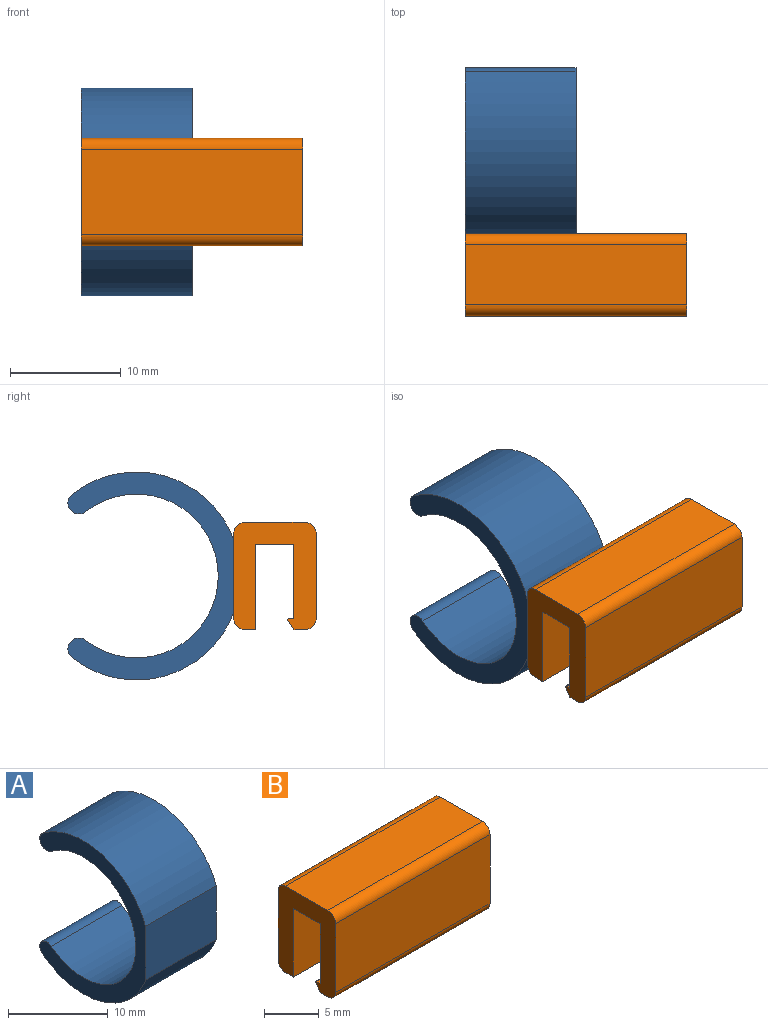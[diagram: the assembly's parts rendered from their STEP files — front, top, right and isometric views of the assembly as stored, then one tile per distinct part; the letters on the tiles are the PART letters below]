
ASSEMBLY  parts=2 mates=1
PART A: 8 faces, bbox 10x15x18.8 mm
  f0: cylinder r=9.4mm len=14.61mm, axis (-1,0,0), area 176.5mm2, adj f3,f4,f5,f7
  f1: cylinder r=9.4mm len=14.61mm, axis (-1,0,0), area 176.5mm2, adj f3,f4,f6,f7
  f2: cylinder r=7.4mm len=14.8mm, axis (-1,0,0), area 331.1mm2, adj f3,f4,f5,f6
  f3: plane 18.8x14.99mm, normal (1,0,0), area 75.6mm2, adj f0,f1,f2,f5,f6,f7
  f4: plane 18.8x14.99mm, normal (-1,0,0), area 75.6mm2, adj f0,f1,f2,f5,f6,f7
  f5: cylinder r=1mm len=10mm, axis (-1,0,0), area 31.4mm2, adj f0,f2,f3,f4
  f6: cylinder r=1mm len=10mm, axis (-1,0,0), area 31.4mm2, adj f1,f2,f3,f4
  f7: plane 10x6.61mm, normal (0,-1,0), area 66.1mm2, adj f0,f1,f3,f4
PART B: 17 faces, bbox 20x7.5x9.7 mm
  f0: plane 20x1mm, normal (0,0,-1), area 20mm2, adj f1,f10,f11,f16
  f1: plane 20x0.85mm, normal (0,0.84,-0.54), area 20.2mm2, adj f0,f10,f11,f12
  f2: plane 20x0.47mm, normal (0,0,1), area 9.3mm2, adj f3,f10,f11,f12
  f3: plane 20x6.7mm, normal (0,1,0), area 134mm2, adj f2,f4,f10,f11
  f4: plane 20x3.45mm, normal (0,0,-1), area 69mm2, adj f3,f5,f10,f11
  f5: plane 20x7.7mm, normal (0,-1,0), area 154mm2, adj f4,f6,f10,f11
  f6: plane 20x1mm, normal (0,0,-1), area 20mm2, adj f5,f10,f11,f13
  f7: plane 20x7.7mm, normal (0,1,0), area 154mm2, adj f10,f11,f13,f14
  f8: plane 20x5.45mm, normal (0,0,1), area 109mm2, adj f10,f11,f14,f15
  f9: plane 20x7.7mm, normal (0,-1,0), area 154mm2, adj f10,f11,f15,f16
  f10: plane 9.7x7.45mm, normal (1,0,0), area 45.2mm2, adj f0,f1,f2,f3,f4,f5,f6,f7
  f11: plane 9.7x7.45mm, normal (-1,0,0), area 45.2mm2, adj f0,f1,f2,f3,f4,f5,f6,f7
  f12: cylinder r=0.1mm len=20mm, axis (-1,0,0), area 4.3mm2, adj f1,f2,f10,f11
  f13: cylinder r=1mm len=20mm, axis (-1,0,0), area 31.4mm2, adj f6,f7,f10,f11
  f14: cylinder r=1mm len=20mm, axis (-1,0,0), area 31.4mm2, adj f7,f8,f10,f11
  f15: cylinder r=1mm len=20mm, axis (1,0,0), area 31.4mm2, adj f8,f9,f10,f11
  f16: cylinder r=1mm len=20mm, axis (-1,0,0), area 31.4mm2, adj f0,f9,f10,f11
PLACE A t=(-15.69,13.08,7.41)mm
PLACE B t=(-10.69,0.56,6.91)mm
MATE fastened B.f7 <-> A.f7  axis (0,1,0) through (-20.69,4.28,7.41)mm
